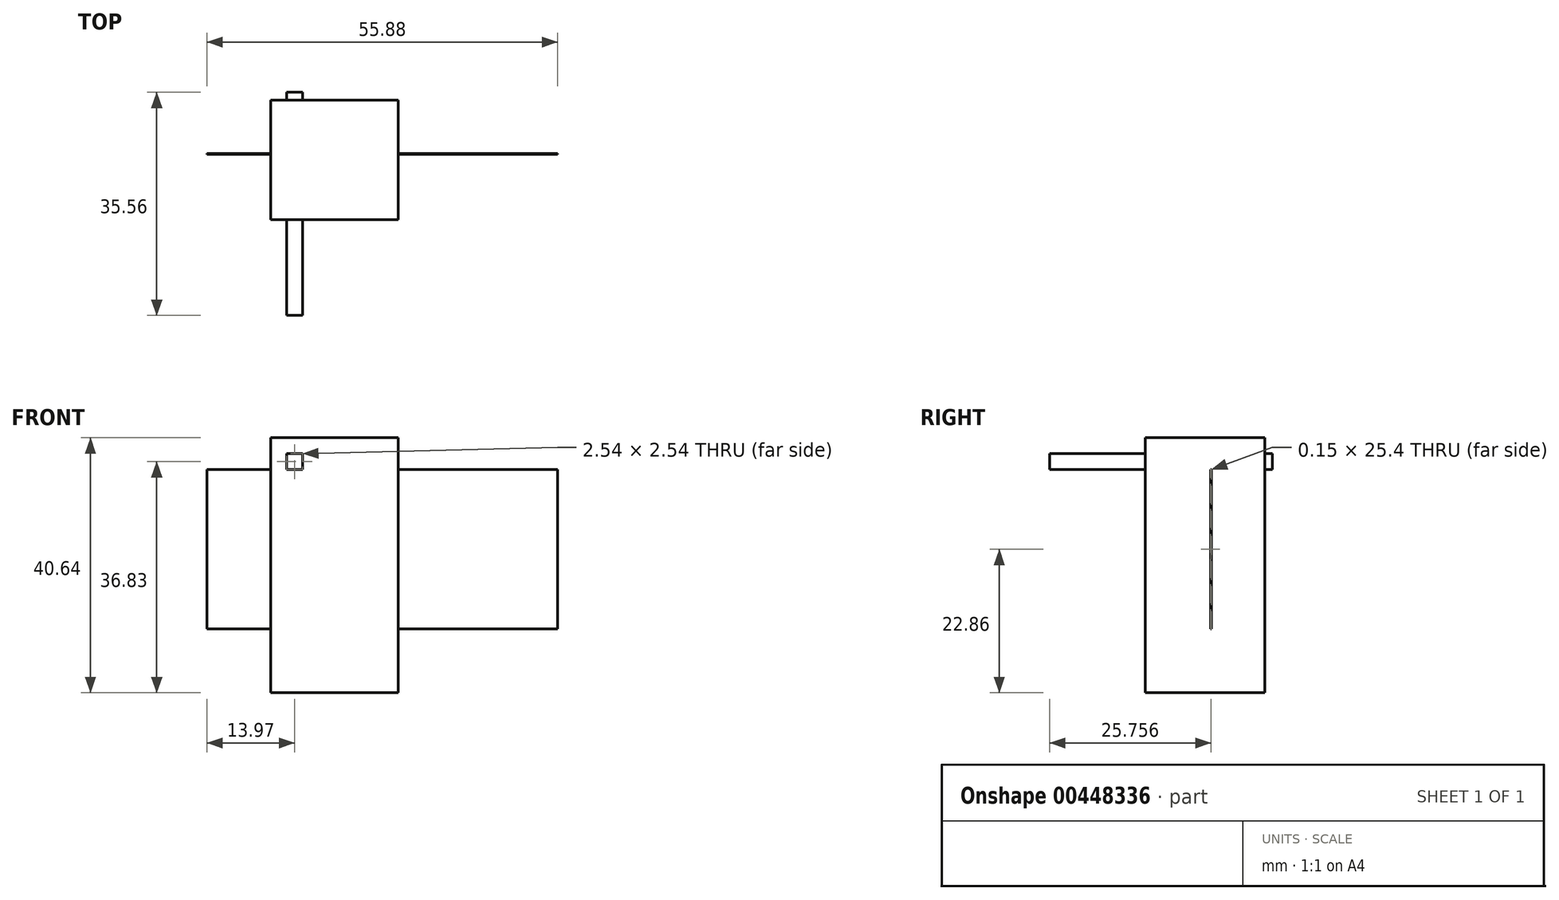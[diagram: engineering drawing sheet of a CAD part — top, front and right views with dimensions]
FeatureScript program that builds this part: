
annotation { "Feature Type Name" : "Feature", "Feature Type Description" : "" }
export const myFeature = defineFeature(function(context is Context, id is Id, definition is map)
    precondition{}
    {
        {
            var Q0;
            Q0=qCreatedBy(makeId("Front.planeOp"),FACE);
            var sketch = newSketch(context, id + "F0", { "sketchPlane" : qUnion([Q0])});
            skLineSegment(sketch, "E0.bottom", {"start": v(0, 0) * mm, "end": v(20.32, 0) * mm});
            skLineSegment(sketch, "E0.top", {"start": v(0, 40.64) * mm, "end": v(20.32, 40.64) * mm});
            skLineSegment(sketch, "E0.left", {"start": v(0, 0) * mm, "end": v(0, 40.64) * mm});
            skLineSegment(sketch, "E0.right", {"start": v(20.32, 0) * mm, "end": v(20.32, 40.64) * mm});
            skSolve(sketch);
        }
        {
            var Q0;
            Q0=makeQuery(id+"F0.imprint","IMPRINT",FACE,{"disambiguationData":[TD([[makeQuery(id+"F0.imprint","IMPRINT",EDGE,{"derivedFrom":sQuery(id+"F0.wireOp",EDGE,"E0.bottom")}),1.0]])]});
            extrude(context, id + "F1", {"entities" : qUnion([Q0]), "depth" : 19.05 * mm});
        }
        {
            var Q0;
            Q0=makeQuery(id+"F1.opExtrude","SWEPT_FACE",FACE,{"disambiguationData":[OSD([sQuery(id+"F0.wireOp",EDGE,"E0.right")])]});
            var sketch = newSketch(context, id + "F2", { "sketchPlane" : qUnion([Q0])});
            skLineSegment(sketch, "E1.bottom", {"start": v(-8.61, 35.56) * mm, "end": v(-8.46, 35.56) * mm});
            skLineSegment(sketch, "E1.top", {"start": v(-8.61, 10.16) * mm, "end": v(-8.46, 10.16) * mm});
            skLineSegment(sketch, "E1.left", {"start": v(-8.61, 35.56) * mm, "end": v(-8.61, 10.16) * mm});
            skLineSegment(sketch, "E1.right", {"start": v(-8.46, 35.56) * mm, "end": v(-8.46, 10.16) * mm});
            skSolve(sketch);
        }
        {
            var Q0;
            Q0 = qSketchRegion(id + "F2", true);
            extrude(context, id + "F3", {"entities" : qUnion([Q0]), "operationType" : NewBodyOperationType.ADD, "depth" : 25.4 * mm, "hasSecondDirection" : true, "secondDirectionOppositeDirection" : true, "secondDirectionDepth" : 30.48 * mm});
        }
        {
            var Q0;
            Q0=makeQuery(id+"F1.opExtrude","CAP_FACE",FACE,{"disambiguationData":[OSD([sQuery(id+"F0.wireOp",EDGE,"E0.bottom"),sQuery(id+"F0.wireOp",EDGE,"E0.top"),sQuery(id+"F0.wireOp",EDGE,"E0.left"),sQuery(id+"F0.wireOp",EDGE,"E0.right")])],"isStart":false});
            var sketch = newSketch(context, id + "F4", { "sketchPlane" : qUnion([Q0])});
            skLineSegment(sketch, "E2.bottom", {"start": v(2.54, 38.1) * mm, "end": v(5.08, 38.1) * mm});
            skLineSegment(sketch, "E2.top", {"start": v(2.54, 35.56) * mm, "end": v(5.08, 35.56) * mm});
            skLineSegment(sketch, "E2.left", {"start": v(2.54, 38.1) * mm, "end": v(2.54, 35.56) * mm});
            skLineSegment(sketch, "E2.right", {"start": v(5.08, 38.1) * mm, "end": v(5.08, 35.56) * mm});
            skSolve(sketch);
        }
        {
            var Q0;
            Q0=makeQuery(id+"F4.imprint","IMPRINT",FACE,{"disambiguationData":[TD([[makeQuery(id+"F4.imprint","IMPRINT",EDGE,{"derivedFrom":sQuery(id+"F4.wireOp",EDGE,"E2.bottom")}),-1.0]])]});
            extrude(context, id + "F5", {"entities" : qUnion([Q0]), "operationType" : NewBodyOperationType.ADD, "depth" : 15.24 * mm, "hasSecondDirection" : true, "secondDirectionOppositeDirection" : true, "secondDirectionDepth" : 20.32 * mm});
        }
    });
